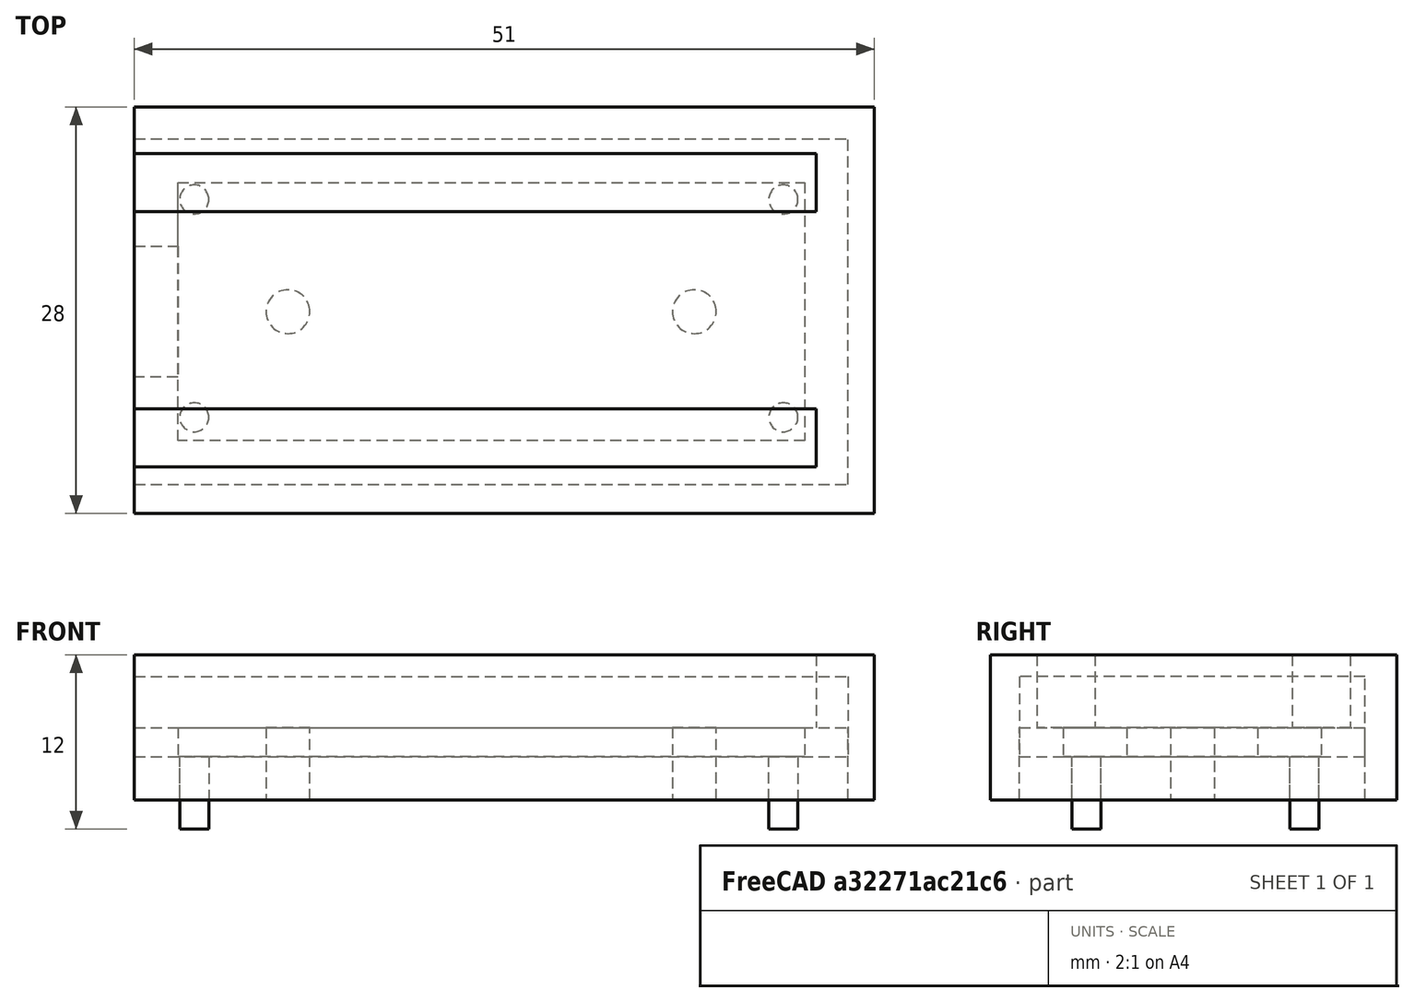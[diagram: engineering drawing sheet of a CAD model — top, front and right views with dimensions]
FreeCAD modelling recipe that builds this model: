
FCSTD DOCUMENT  (FreeCAD 0.14R2935 (Git))
Label: soporteArduinoNano
License: CC-BY 3.0
LicenseURL: http://creativecommons.org/licenses/by/3.0/
objects: PartDesign::Pocket×7, Sketcher::SketchObject×6, Part::Box×2, Part::Cut×1, Mesh::Feature×1
note: 23 computed .brp shape members not serialized (recipe doc carries the construction recipe); baked Part::Feature solids carry a one-line shape summary decoded from their .brp

FEATURE [Part::Box] Box
  Height = 5
  Length = 49.18
  Width = 23.8
FEATURE [Sketcher::SketchObject] Sketch
  Placement = pos=(0,0,5) rot=(0,0,1;0rad)
  Support = -> Box [Face6]
  sketch-geometry (4):
    g0: LineSegment StartX=3 StartY=20.8 StartZ=0 EndX=46.2 EndY=20.8 EndZ=0
    g1: LineSegment StartX=46.2 StartY=20.8 StartZ=0 EndX=46.2 EndY=3 EndZ=0
    g2: LineSegment StartX=46.2 StartY=3 StartZ=0 EndX=3 EndY=3 EndZ=0
    g3: LineSegment StartX=3 StartY=3 StartZ=0 EndX=3 EndY=20.8 EndZ=0
  constraints (12):
    c: Coincident(g0,g1)
    c: Coincident(g1,g2)
    c: Coincident(g2,g3)
    c: Coincident(g3,g0)
    c: Horizontal(g0)
    c: Horizontal(g2)
    c: Vertical(g1)
    c: Vertical(g3)
    c: DistanceX(g0) = 43.2
    c: DistanceY(g1) = -17.8
    c: DistanceY(g-1,g2) = 3
    c: DistanceX(g-2,g0) = 3
FEATURE [PartDesign::Pocket] Pocket
  Length = 2
  Sketch = -> Sketch
  Type = 0
FEATURE [Sketcher::SketchObject] Sketch001
  ExternalGeometry = -> [Pocket]
  Placement = pos=(0,0,5) rot=(0,0,1;0rad)
  Support = -> Pocket [Face3]
  sketch-geometry (6):
    g0: LineSegment StartX=0 StartY=16.4 StartZ=0 EndX=3 EndY=16.4 EndZ=0
    g1: LineSegment StartX=3 StartY=16.4 StartZ=0 EndX=3 EndY=7.4 EndZ=0
    g2: LineSegment StartX=3 StartY=7.4 StartZ=0 EndX=0 EndY=7.4 EndZ=0
    g3: LineSegment StartX=0 StartY=7.4 StartZ=0 EndX=0 EndY=16.4 EndZ=0
    g4: LineSegment [constr] StartX=3 StartY=20.8 StartZ=0 EndX=3 EndY=16.4 EndZ=0
    g5: LineSegment [constr] StartX=3 StartY=7.4 StartZ=0 EndX=3 EndY=3 EndZ=0
  constraints (18):
    c: Coincident(g0,g1)
    c: Coincident(g1,g2)
    c: Coincident(g2,g3)
    c: Coincident(g3,g0)
    c: Horizontal(g0)
    c: Horizontal(g2)
    c: Vertical(g1)
    c: Vertical(g3)
    c: DistanceY(g3) = 9
    c: PointOnObject(g0,g-3)
    c: PointOnObject(g0,g-2)
    c: Vertical(g5)
    c: Vertical(g4)
    c: Equal(g4,g5)
    c: Coincident(g4,g-3)
    c: Coincident(g0,g4)
    c: Coincident(g5,g1)
    c: Coincident(g5,g-3)
FEATURE [PartDesign::Pocket] Pocket001
  Length = 2
  Sketch = -> Sketch001
  Type = 0
FEATURE [Part::Box] Box001
  Height = 10
  Length = 51
  Placement = pos=(0,-2,0) rot=(0,0,1;0rad)
  Width = 28
FEATURE [PartDesign::Pocket] Pocket002
  Length = 2
  Sketch = -> Sketch001
  Type = 0
FEATURE [Part::Cut] Cut
  Base = -> Box001
  Tool = -> Pocket002
FEATURE [Sketcher::SketchObject] Sketch002
  ExternalGeometry = -> [Cut]
  Placement = pos=(0,0,0) rot=(0.57735,-0.57735,-0.57735;2.0944rad)
  Support = -> Cut [Face1]
  sketch-geometry (4):
    g0: LineSegment StartX=-23.8 StartY=8.5 StartZ=0 EndX=0 EndY=8.5 EndZ=0
    g1: LineSegment StartX=0 StartY=8.5 StartZ=0 EndX=0 EndY=3 EndZ=0
    g2: LineSegment StartX=0 StartY=3 StartZ=0 EndX=-23.8 EndY=3 EndZ=0
    g3: LineSegment StartX=-23.8 StartY=3 StartZ=0 EndX=-23.8 EndY=8.5 EndZ=0
  constraints (12):
    c: Coincident(g0,g1)
    c: Coincident(g1,g2)
    c: Coincident(g2,g3)
    c: Coincident(g3,g0)
    c: Horizontal(g0)
    c: Horizontal(g2)
    c: Vertical(g1)
    c: Vertical(g3)
    c: PointOnObject(g1,g-2)
    c: PointOnObject(g-4,g2)
    c: PointOnObject(g2,g-3)
    c: Distance(g0,g-5) = 1.5
FEATURE [PartDesign::Pocket] Pocket003
  Length = 49.18
  Sketch = -> Sketch002
  Type = 0
FEATURE [Sketcher::SketchObject] Sketch003
  ExternalGeometry = -> [Pocket003]
  Placement = pos=(0,0,10) rot=(0,0,1;0rad)
  Support = -> Pocket003 [Face12]
  sketch-geometry (9):
    g0: LineSegment StartX=0 StartY=22.8 StartZ=0 EndX=47 EndY=22.8 EndZ=0
    g1: LineSegment StartX=47 StartY=22.8 StartZ=0 EndX=47 EndY=18.8 EndZ=0
    g2: LineSegment StartX=47 StartY=18.8 StartZ=0 EndX=0 EndY=18.8 EndZ=0
    g3: LineSegment StartX=0 StartY=18.8 StartZ=0 EndX=0 EndY=22.8 EndZ=0
    g4: LineSegment StartX=0 StartY=5.2 StartZ=0 EndX=47 EndY=5.2 EndZ=0
    g5: LineSegment StartX=47 StartY=5.2 StartZ=0 EndX=47 EndY=1.2 EndZ=0
    g6: LineSegment StartX=47 StartY=1.2 StartZ=0 EndX=0 EndY=1.2 EndZ=0
    g7: LineSegment StartX=0 StartY=1.2 StartZ=0 EndX=0 EndY=5.2 EndZ=0
    g8: LineSegment [constr] StartX=47 StartY=26 StartZ=0 EndX=47 EndY=-2 EndZ=0
  constraints (28):
    c: Coincident(g0,g1)
    c: Coincident(g1,g2)
    c: Coincident(g2,g3)
    c: Coincident(g3,g0)
    c: Horizontal(g0)
    c: Horizontal(g2)
    c: Vertical(g1)
    c: Vertical(g3)
    c: Coincident(g4,g5)
    c: Coincident(g5,g6)
    c: Coincident(g6,g7)
    c: Coincident(g7,g4)
    c: Horizontal(g4)
    c: Horizontal(g6)
    c: Vertical(g5)
    c: Vertical(g7)
    c: Equal(g7,g3)
    c: DistanceY(g7) = 4
    c: PointOnObject(g2,g-2)
    c: PointOnObject(g4,g-2)
    c: Vertical(g8)
    c: PointOnObject(g8,g-4)
    c: PointOnObject(g8,g-3)
    c: PointOnObject(g1,g8)
    c: PointOnObject(g4,g8)
    c: Distance(g-3,g0) = 3.2
    c: Distance(g6,g-4) = 3.2
    c: Distance(g8,g-4) = 4
FEATURE [PartDesign::Pocket] Pocket004
  Length = 5
  Sketch = -> Sketch003
  Type = 0
FEATURE [Mesh::Feature] arduino_nano
  Placement = pos=(90,-19,4) rot=(0,0,1;1.5708rad)
FEATURE [Sketcher::SketchObject] Sketch004
  Placement = pos=(0,0,3) rot=(0,0,1;0rad)
  Support = -> Pocket001 [Face15]
  sketch-geometry (8):
    g0: Circle CenterX=44.7222 CenterY=19.6345 CenterZ=0 NormalX=0 NormalY=0 NormalZ=1 Radius=1
    g1: Circle CenterX=44.7222 CenterY=4.6221 CenterZ=0 NormalX=0 NormalY=0 NormalZ=1 Radius=1
    g2: Circle CenterX=4.13319 CenterY=19.6345 CenterZ=0 NormalX=0 NormalY=0 NormalZ=1 Radius=1
    g3: Circle CenterX=4.13319 CenterY=4.6221 CenterZ=0 NormalX=0 NormalY=0 NormalZ=1 Radius=1
    g4: LineSegment [constr] StartX=4.13319 StartY=19.6345 StartZ=0 EndX=44.7222 EndY=19.6345 EndZ=0
    g5: LineSegment [constr] StartX=44.7222 StartY=19.6345 StartZ=0 EndX=44.7222 EndY=4.6221 EndZ=0
    g6: LineSegment [constr] StartX=44.7222 StartY=4.6221 StartZ=0 EndX=4.13319 EndY=4.6221 EndZ=0
    g7: LineSegment [constr] StartX=4.13319 StartY=4.6221 StartZ=0 EndX=4.13319 EndY=19.6345 EndZ=0
  constraints (16):
    c: Equal(g3,g2)
    c: Equal(g2,g0)
    c: Equal(g0,g1)
    c: Radius(g2) = 1
    c: Coincident(g4,g5)
    c: Coincident(g5,g6)
    c: Coincident(g6,g7)
    c: Coincident(g7,g4)
    c: Horizontal(g4)
    c: Horizontal(g6)
    c: Vertical(g5)
    c: Vertical(g7)
    c: Coincident(g2,g4)
    c: Coincident(g0,g4)
    c: Coincident(g5,g1)
    c: Coincident(g3,g6)
FEATURE [PartDesign::Pocket] Pocket005
  Length = 5
  Sketch = -> Sketch004
  Type = 0
FEATURE [Sketcher::SketchObject] Sketch005
  ExternalGeometry = -> [Pocket005]
  Placement = pos=(0,0,0) rot=(1,0,0;3.14159rad)
  Support = -> Pocket005 [Face7]
  sketch-geometry (7):
    g0: LineSegment [constr] StartX=0 StartY=-11.9 StartZ=0 EndX=49.18 EndY=-11.9 EndZ=0
    g1: Circle CenterX=10.59 CenterY=-11.9 CenterZ=0 NormalX=0 NormalY=0 NormalZ=1 Radius=1.51127
    g2: Circle CenterX=38.59 CenterY=-11.9 CenterZ=0 NormalX=0 NormalY=0 NormalZ=1 Radius=1.51127
    g3: LineSegment [constr] StartX=0 StartY=0 StartZ=0 EndX=0 EndY=-11.9 EndZ=0
    g4: LineSegment [constr] StartX=0 StartY=-11.9 StartZ=0 EndX=0 EndY=-23.8 EndZ=0
    g5: LineSegment [constr] StartX=0 StartY=-11.9 StartZ=0 EndX=10.59 EndY=-11.9 EndZ=0
    g6: LineSegment [constr] StartX=38.59 StartY=-11.9 StartZ=0 EndX=49.18 EndY=-11.9 EndZ=0
  constraints (20):
    c: PointOnObject(g1,g0)
    c: PointOnObject(g2,g0)
    c: Distance(g1,g2) = 28
    c: Equal(g1,g2)
    c: Radius(g2) = 1.51127
    c: Vertical(g3)
    c: Vertical(g4)
    c: Equal(g3,g4)
    c: Coincident(g4,g-3)
    c: Coincident(g3,g-1)
    c: Coincident(g3,g0)
    c: Coincident(g0,g4)
    c: PointOnObject(g0,g-4)
    c: Horizontal(g5)
    c: Horizontal(g6)
    c: Equal(g5,g6)
    c: Coincident(g6,g0)
    c: Coincident(g6,g2)
    c: Coincident(g5,g1)
    c: Coincident(g5,g0)
FEATURE [PartDesign::Pocket] Pocket006
  Length = 5
  Sketch = -> Sketch005
  Type = 0
